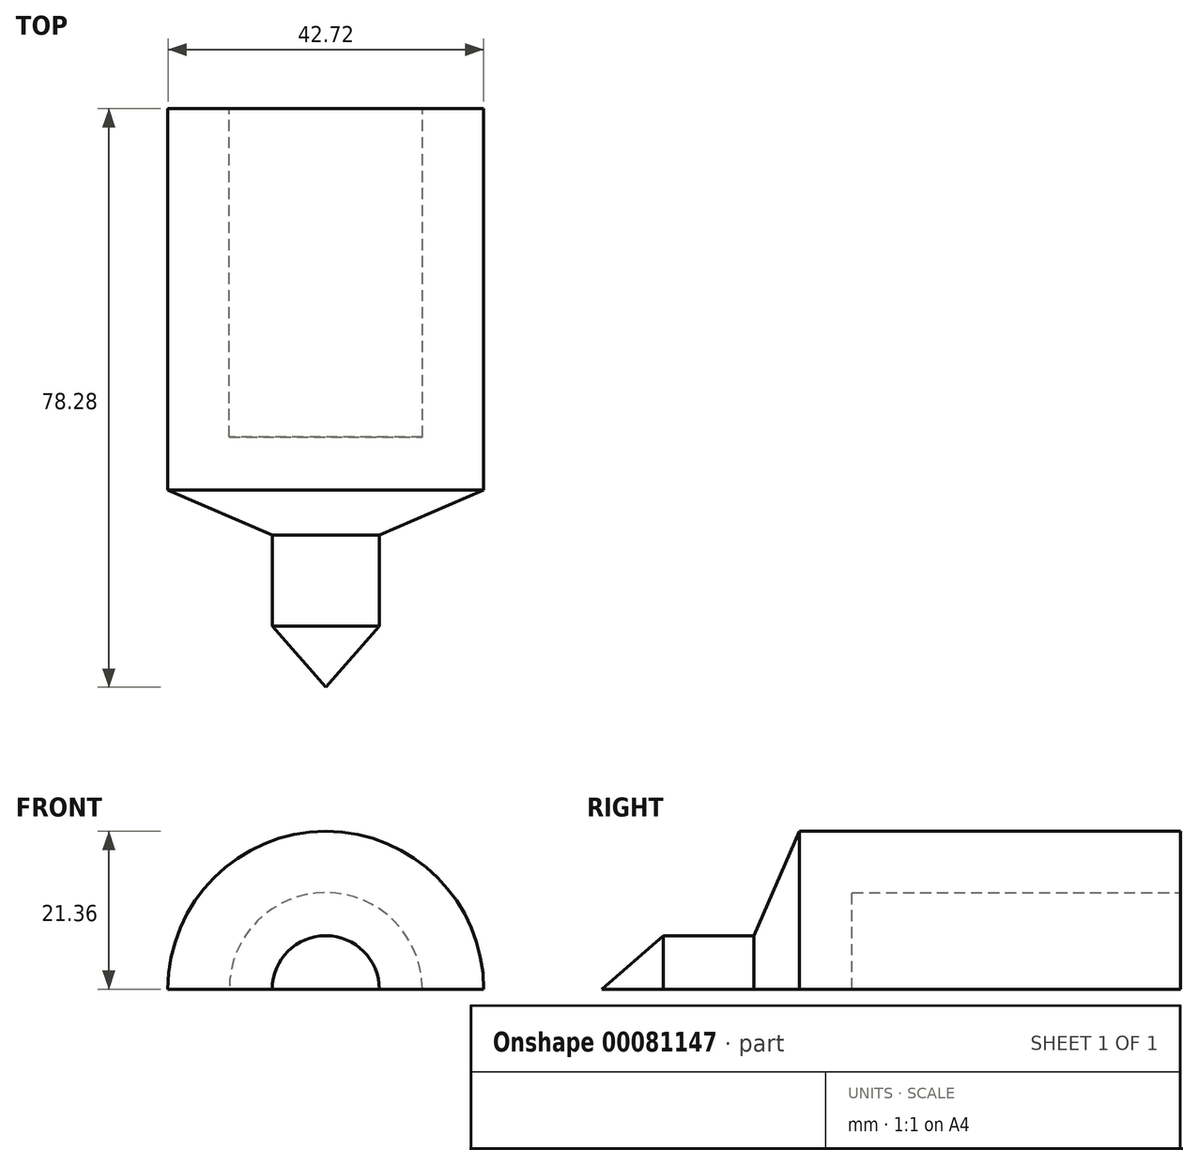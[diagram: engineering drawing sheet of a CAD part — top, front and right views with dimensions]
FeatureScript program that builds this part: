
annotation { "Feature Type Name" : "Feature", "Feature Type Description" : "" }
export const myFeature = defineFeature(function(context is Context, id is Id, definition is map)
    precondition{}
    {
        {
            var Q0;
            Q0=qCreatedBy(makeId("Top.planeOp"),FACE);
            var sketch = newSketch(context, id + "F0", { "sketchPlane" : qUnion([Q0])});
            skLineSegment(sketch, "E0.bottom", {"start": v(-127, 127) * mm, "end": v(127, 127) * mm});
            skLineSegment(sketch, "E0.top", {"start": v(-127, -127) * mm, "end": v(127, -127) * mm});
            skLineSegment(sketch, "E0.left", {"start": v(-127, 127) * mm, "end": v(-127, -127) * mm});
            skLineSegment(sketch, "E0.right", {"start": v(127, 127) * mm, "end": v(127, -127) * mm});
            skLineSegment(sketch, "E1", {"start": v(-127, 127) * mm, "end": v(127, -127) * mm, "construction": true});
            skLineSegment(sketch, "E2", {"start": v(127, 127) * mm, "end": v(-127, -127) * mm, "construction": true});
            skSolve(sketch);
        }
        {
            var Q0;
            Q0 = qSketchRegion(id + "F0", true);
            extrude(context, id + "F1", {"entities" : qUnion([Q0]), "depth" : 82.87 * mm});
        }
        {
            var Q0;
            Q0=qCreatedBy(makeId("Right.planeOp"),FACE);
            var sketch = newSketch(context, id + "F2", { "sketchPlane" : qUnion([Q0])});
            skLineSegment(sketch, "E3", {"start": v(-35.48, 0) * mm, "end": v(-27.2, 7.24) * mm});
            skLineSegment(sketch, "E4", {"start": v(-27.2, 7.24) * mm, "end": v(-14.91, 7.24) * mm});
            skLineSegment(sketch, "E5", {"start": v(-14.91, 7.24) * mm, "end": v(-8.77, 21.36) * mm});
            skLineSegment(sketch, "E6", {"start": v(-8.77, 21.36) * mm, "end": v(42.8, 21.36) * mm});
            skLineSegment(sketch, "E7", {"start": v(42.8, 21.36) * mm, "end": v(42.8, 0) * mm});
            skLineSegment(sketch, "E8", {"start": v(42.8, 0) * mm, "end": v(-35.48, 0) * mm});
            skSolve(sketch);
        }
        {
            var Q0;
            Q0 = qSketchRegion(id + "F2", true);
            var Q1;
            Q1=sQuery(id+"F2.wireOp",EDGE,"E8");
            revolve(context, id + "F3", {"entities" : qUnion([Q0]), "axis" : qUnion([Q1]), "revolveType" : RevolveType.FULL});
        }
        {
            var Q0;
            Q0=makeQuery(id+"F3.opRevolve","SWEPT_FACE",FACE,{"disambiguationData":[OSD([sQuery(id+"F2.wireOp",EDGE,"E7")])]});
            var sketch = newSketch(context, id + "F4", { "sketchPlane" : qUnion([Q0])});
            skCircle(sketch, "E9.0", {"center": v(0, 0) * mm, "radius": 21.36 * mm, "construction": true});
            skCircle(sketch, "E10", {"center": v(0, 0) * mm, "radius": 13.06 * mm});
            skSolve(sketch);
        }
        {
            var Q0;
            Q0 = qSketchRegion(id + "F4", true);
            extrude(context, id + "F5", {"entities" : qUnion([Q0]), "operationType" : NewBodyOperationType.REMOVE, "oppositeDirection" : true, "depth" : 44.43 * mm});
        }
        {
            var Q0;
            Q0=makeQuery(id+"F1.opExtrude","SWEPT_BODY",BODY,{"disambiguationData":[OSD([sQuery(id+"F0.wireOp",EDGE,"E0.bottom"),sQuery(id+"F0.wireOp",EDGE,"E0.top"),sQuery(id+"F0.wireOp",EDGE,"E0.left"),sQuery(id+"F0.wireOp",EDGE,"E0.right")])]});
            var Q1;
            Q1=makeQuery(id+"F3.opRevolve","SWEPT_BODY",BODY,{"disambiguationData":[OSD([sQuery(id+"F2.wireOp",EDGE,"E3"),sQuery(id+"F2.wireOp",EDGE,"E4"),sQuery(id+"F2.wireOp",EDGE,"E5"),sQuery(id+"F2.wireOp",EDGE,"E6"),sQuery(id+"F2.wireOp",EDGE,"E7"),sQuery(id+"F2.wireOp",EDGE,"E8")])]});
            booleanBodies(context, id + "F6", {"operationType" : BooleanOperationType.INTERSECTION, "tools" : qUnion([Q0, Q1])});
        }
    });
